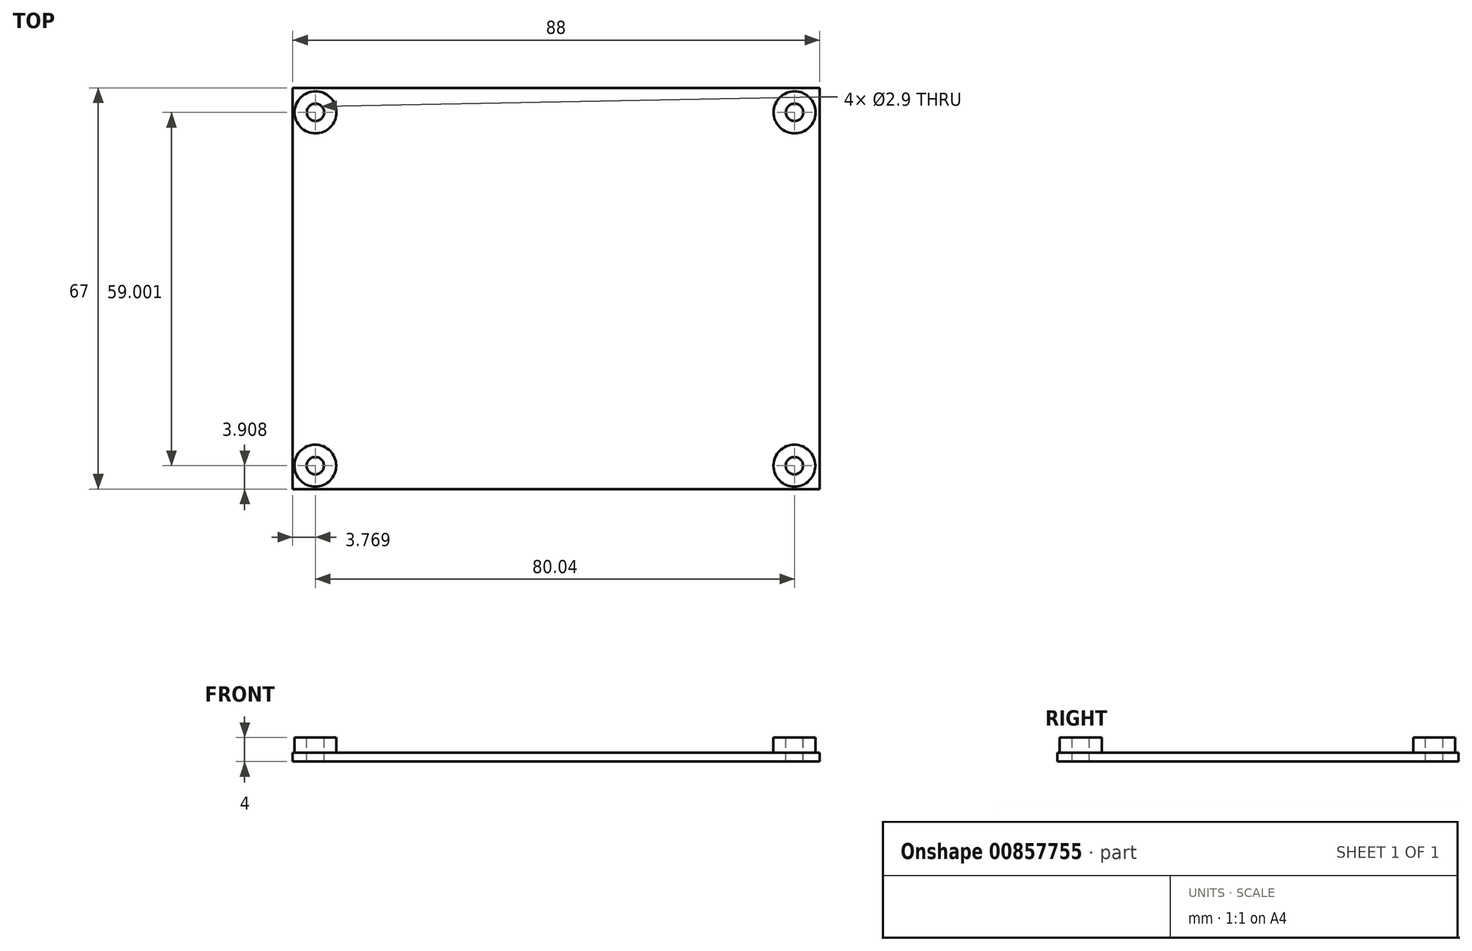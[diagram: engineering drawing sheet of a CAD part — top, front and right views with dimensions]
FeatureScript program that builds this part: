
annotation { "Feature Type Name" : "Feature", "Feature Type Description" : "" }
export const myFeature = defineFeature(function(context is Context, id is Id, definition is map)
    precondition{}
    {
        {
            var Q0;
            Q0=qCreatedBy(makeId("Top.planeOp"),FACE);
            var sketch = newSketch(context, id + "F0", { "sketchPlane" : qUnion([Q0])});
            skLineSegment(sketch, "E0.bottom", {"start": v(-44, 32.58) * mm, "end": v(44, 32.58) * mm});
            skLineSegment(sketch, "E0.top", {"start": v(-44, -34.42) * mm, "end": v(44, -34.42) * mm});
            skLineSegment(sketch, "E0.left", {"start": v(-44, 32.58) * mm, "end": v(-44, -34.42) * mm});
            skLineSegment(sketch, "E0.right", {"start": v(44, 32.58) * mm, "end": v(44, -34.42) * mm});
            skPoint(sketch, "E0.middle", {"position": v(0, -0.92) * mm});
            skSolve(sketch);
        }
        {
            var Q0;
            Q0=makeQuery(id+"F0.imprint","IMPRINT",FACE,{"disambiguationData":[TD([[makeQuery(id+"F0.imprint","IMPRINT",EDGE,{"derivedFrom":sQuery(id+"F0.wireOp",EDGE,"E0.bottom")}),-1.0]])]});
            extrude(context, id + "F1", {"entities" : qUnion([Q0]), "depth" : 1.5 * mm, "offsetDistance" : 25 * mm});
        }
        {
            var Q0;
            Q0=makeQuery(id+"F0.imprint","IMPRINT",FACE,{"disambiguationData":[TD([[makeQuery(id+"F0.imprint","IMPRINT",EDGE,{"derivedFrom":sQuery(id+"F0.wireOp",EDGE,"E0.bottom")}),-1.0]])]});
            var sketch = newSketch(context, id + "F2", { "sketchPlane" : qUnion([Q0])});
            skCircle(sketch, "E1", {"center": v(39.77, -30.51) * mm, "radius": 3.5 * mm});
            skCircle(sketch, "E2", {"center": v(39.8, 28.49) * mm, "radius": 3.5 * mm});
            skCircle(sketch, "E3", {"center": v(-40.23, -30.51) * mm, "radius": 3.5 * mm});
            skCircle(sketch, "E4", {"center": v(-40.2, 28.49) * mm, "radius": 3.5 * mm});
            skSolve(sketch);
        }
        {
            var Q0;
            Q0=makeQuery(id+"F2.imprint","IMPRINT",FACE,{"disambiguationData":[TD([[makeQuery(id+"F2.imprint","IMPRINT",EDGE,{"derivedFrom":sQuery(id+"F2.wireOp",EDGE,"E4")}),1.0]])]});
            var Q1;
            Q1=makeQuery(id+"F2.imprint","IMPRINT",FACE,{"disambiguationData":[TD([[makeQuery(id+"F2.imprint","IMPRINT",EDGE,{"derivedFrom":sQuery(id+"F2.wireOp",EDGE,"E2")}),1.0]])]});
            var Q2;
            Q2=makeQuery(id+"F2.imprint","IMPRINT",FACE,{"disambiguationData":[TD([[makeQuery(id+"F2.imprint","IMPRINT",EDGE,{"derivedFrom":sQuery(id+"F2.wireOp",EDGE,"E3")}),1.0]])]});
            var Q3;
            Q3=makeQuery(id+"F2.imprint","IMPRINT",FACE,{"disambiguationData":[TD([[makeQuery(id+"F2.imprint","IMPRINT",EDGE,{"derivedFrom":sQuery(id+"F2.wireOp",EDGE,"E1")}),1.0]])]});
            var Q4;
            Q4=sQuery(id+"F2.wireOp",EDGE,"E2");
            var Q5;
            Q5=sQuery(id+"F2.wireOp",EDGE,"E4");
            var Q6;
            Q6=sQuery(id+"F2.wireOp",EDGE,"E1");
            var Q7;
            Q7=sQuery(id+"F2.wireOp",EDGE,"E3");
            extrude(context, id + "F3", {"entities" : qUnion([Q0, Q1, Q2, Q3]), "operationType" : NewBodyOperationType.ADD, "surfaceOperationType" : NewSurfaceOperationType.ADD, "surfaceEntities" : qUnion([Q4, Q5, Q6, Q7]), "depth" : 4 * mm, "offsetDistance" : 25 * mm});
        }
        {
            var Q0;
            Q0=makeQuery(id+"F3.opExtrude","CAP_FACE",FACE,{"disambiguationData":[OSD([sQuery(id+"F2.wireOp",EDGE,"E3")])],"isStart":false});
            var sketch = newSketch(context, id + "F4", { "sketchPlane" : qUnion([Q0])});
            skCircle(sketch, "E5", {"center": v(-40.23, -30.51) * mm, "radius": 1.45 * mm});
            skSolve(sketch);
        }
        {
            var Q0;
            Q0=makeQuery(id+"F3.opExtrude","CAP_FACE",FACE,{"disambiguationData":[OSD([sQuery(id+"F2.wireOp",EDGE,"E4")])],"isStart":false});
            var sketch = newSketch(context, id + "F5", { "sketchPlane" : qUnion([Q0])});
            skCircle(sketch, "E6", {"center": v(-40.2, 28.49) * mm, "radius": 1.45 * mm});
            skSolve(sketch);
        }
        {
            var Q0;
            Q0=makeQuery(id+"F3.opExtrude","CAP_FACE",FACE,{"disambiguationData":[OSD([sQuery(id+"F2.wireOp",EDGE,"E1")])],"isStart":false});
            var sketch = newSketch(context, id + "F6", { "sketchPlane" : qUnion([Q0])});
            skCircle(sketch, "E7", {"center": v(39.77, -30.51) * mm, "radius": 1.45 * mm});
            skSolve(sketch);
        }
        {
            var Q0;
            Q0=makeQuery(id+"F3.opExtrude","CAP_FACE",FACE,{"disambiguationData":[OSD([sQuery(id+"F2.wireOp",EDGE,"E2")])],"isStart":false});
            var sketch = newSketch(context, id + "F7", { "sketchPlane" : qUnion([Q0])});
            skCircle(sketch, "E8", {"center": v(39.8, 28.49) * mm, "radius": 1.45 * mm});
            skSolve(sketch);
        }
        {
            var Q0;
            Q0=makeQuery(id+"F4.imprint","IMPRINT",FACE,{"disambiguationData":[TD([[makeQuery(id+"F4.imprint","IMPRINT",EDGE,{"derivedFrom":sQuery(id+"F4.wireOp",EDGE,"E5")}),1.0]])]});
            var Q1;
            Q1=makeQuery(id+"F5.imprint","IMPRINT",FACE,{"disambiguationData":[TD([[makeQuery(id+"F5.imprint","IMPRINT",EDGE,{"derivedFrom":sQuery(id+"F5.wireOp",EDGE,"E6")}),1.0]])]});
            var Q2;
            Q2=makeQuery(id+"F6.imprint","IMPRINT",FACE,{"disambiguationData":[TD([[makeQuery(id+"F6.imprint","IMPRINT",EDGE,{"derivedFrom":sQuery(id+"F6.wireOp",EDGE,"E7")}),1.0]])]});
            var Q3;
            Q3=makeQuery(id+"F7.imprint","IMPRINT",FACE,{"disambiguationData":[TD([[makeQuery(id+"F7.imprint","IMPRINT",EDGE,{"derivedFrom":sQuery(id+"F7.wireOp",EDGE,"E8")}),1.0]])]});
            extrude(context, id + "F8", {"entities" : qUnion([Q0, Q1, Q2, Q3]), "operationType" : NewBodyOperationType.REMOVE, "oppositeDirection" : true, "depth" : 5 * mm, "offsetDistance" : 25 * mm});
        }
    });
